# Revit family: EX3720 Complete Door - DraftA
name_source: partatom
category: Doors
units: mm (PartAtom-declared; Revit-internal decimal feet)

## family parameters
Always vertical = Yes
Cut with Voids When Loaded = No
Host = Wall
OmniClass Number = 23.30.10.17.37.14
OmniClass Title = Sectional Overhead Doors
Room Calculation Point = No
Shared = No

## types (1)
- By Type
    Assembly Code = B2030410
    CAD and Specifications = http://www.clopaydoor.com
    Color = White
    Control Box - Left Side = No
    Control Box - Right Side = Yes
    Core Material = Expanded polyurethane
    Description = 1-3/8'' thick polyurethane insulated, stucco embossed 27 gauge steel exterior with light ribbed pattern.
    Door Height = 14' - 0"
    Door Width = 14' - 4"
    Double End Stiles = Yes
    Exterior Steel = 27 ga. galvanized, primed, and finish painted
    File Revision = 02 (August, 2012)
    FloorToSection2 = 2' - 0"
    FloorToSection3 = 4' - 0"
    FloorToSection4 = 6' - 0"
    FloorToSection5 = 8' - 0"
    FloorToSection6 = 10' - 0"
    FloorToSection7 = 12' - 0"
    Function = Interior
    GreenFormat = http://www.greenformat.com
    Hardware = 14 ga. min. steel hinges; 10-ball steel rollers
    Height = 14' - 0"
    High Lift = 4' - 0"
    Interior Steel = 27 ga. galvanized, primed, and finish painted
    Keynote = 08 36 13
    LEED = http://products.construction.com
    Manufacturer = Clopay Building Products Company
    Manufacturer Website = http://www.clopaydoor.com
    Maximum High Lift = 10' 0''
    Maximum Size = 16' 2'' wide x 14' 0'' high
    Minimum Size = 8' 0'' wide x 7' 0'' high
    Model = 3715
    NumArraySections = 2
    NumSections = 7
    NumSectionsNotRounded = 7
    Omniclass Table = 23-30 10 17 37
    Opener - Left Side = No
    Opener - Right Side = Yes
    Opening Height = 14' - 0"
    Opening Width = 14' - 2"
    Overlap = 0' - 1"
    Overlapping Jamb = Yes
    Product Features and Benefits = http://www.clopaydoor.com
    R-Value = 17.2
    Rough Height = 0' - 0"
    Rough Width = 0' - 0"
    Sales Information = http://www.clopaydoor.com
    Section 3 Glazing = Full Vision Section : Intermediate
    Section 4 Glazing = Section : Solid
    Section 5 Glazing = Section : Solid
    Section Height = 2' - 0"
    Spec Wizard = http://www.arcat.com
    Thickness = 0' - 2"
    Track = Galvanized steel (gauge varies according to door size)
    Track Type = Track - Standard Lift : 15" Radius
    URL = www.clopaydoor.com
    VisArray = Yes
    VisSection3 = Yes
    VisSection4 = Yes
    VisSection5 = Yes
    VisSection6 = No
    Wall Closure = By host
    Width = 14' - 2"
    Windload = Doors available rated for various design pressures; consult Clopay for avaialbility and specifications

## geometry (parser evidence)
native form markers: Sweep x24
no freeform markers — native parametric forms only
